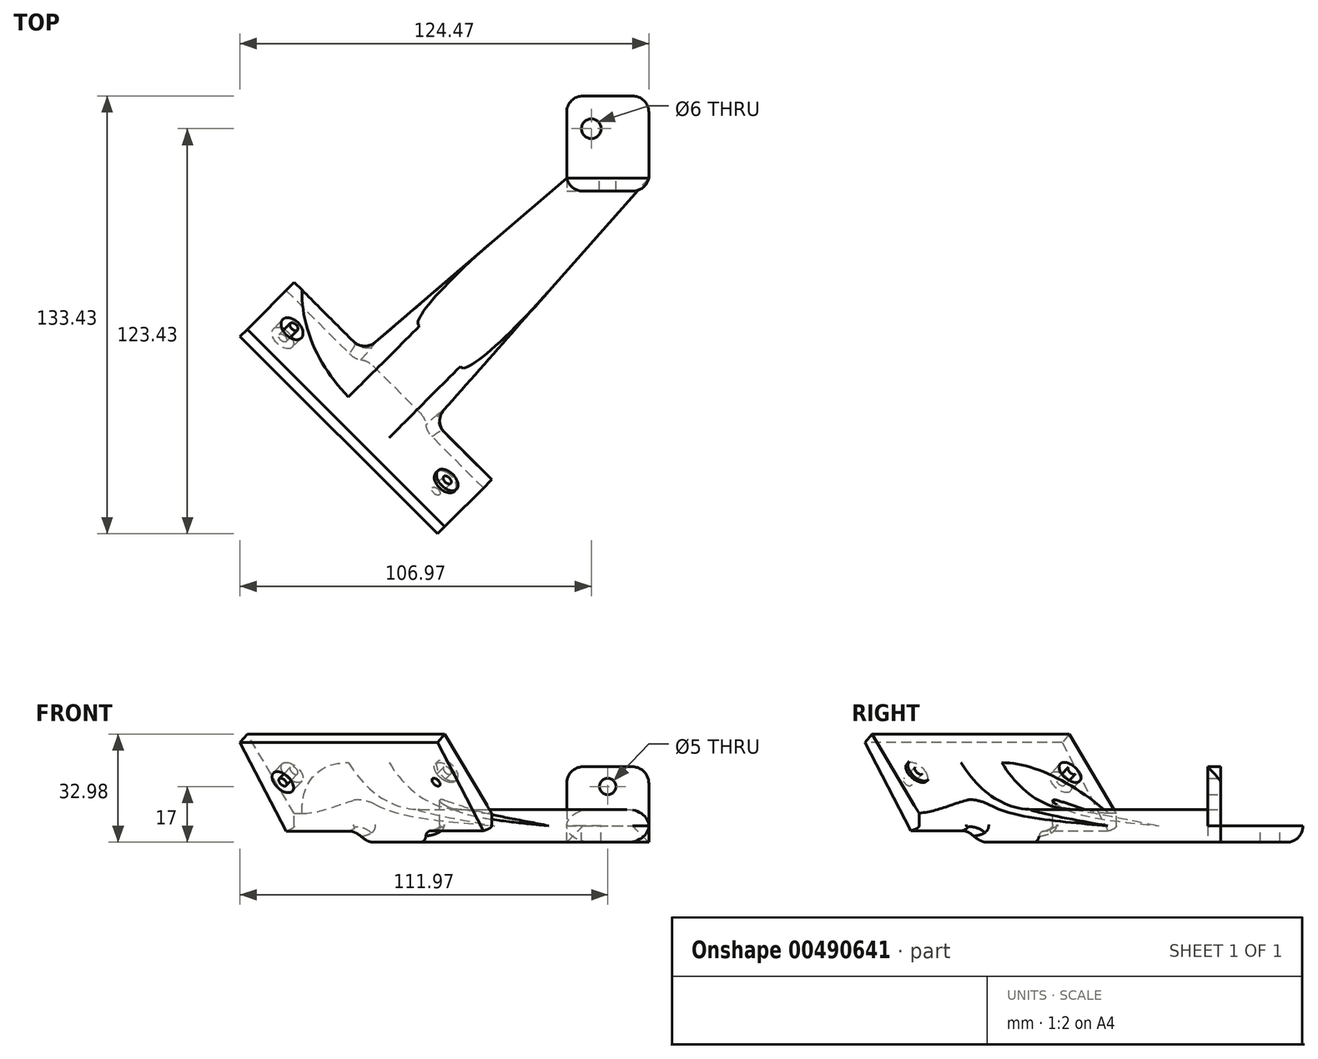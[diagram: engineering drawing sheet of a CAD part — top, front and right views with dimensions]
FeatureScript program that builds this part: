
annotation { "Feature Type Name" : "Feature", "Feature Type Description" : "" }
export const myFeature = defineFeature(function(context is Context, id is Id, definition is map)
    precondition{}
    {
        {
            var Q0;
            Q0=qCreatedBy(makeId("Top.planeOp"),FACE);
            var sketch = newSketch(context, id + "F0", { "sketchPlane" : qUnion([Q0])});
            skLineSegment(sketch, "E0.bottom", {"start": v(-12.5, 0) * mm, "end": v(12.5, 0) * mm});
            skLineSegment(sketch, "E0.top", {"start": v(-12.5, 25) * mm, "end": v(12.5, 25) * mm});
            skLineSegment(sketch, "E0.left", {"start": v(-12.5, 0) * mm, "end": v(-12.5, 25) * mm});
            skLineSegment(sketch, "E0.right", {"start": v(12.5, 0) * mm, "end": v(12.5, 25) * mm});
            skCircle(sketch, "E1", {"center": v(-5, 15) * mm, "radius": 3 * mm});
            skLineSegment(sketch, "E2.top", {"start": v(-12.5, -4) * mm, "end": v(12.5, -4) * mm});
            skLineSegment(sketch, "E2.left", {"start": v(-12.5, 0) * mm, "end": v(-12.5, -4) * mm});
            skLineSegment(sketch, "E2.right", {"start": v(12.5, 0) * mm, "end": v(12.5, -4) * mm});
            skSolve(sketch);
        }
        {
            var Q0;
            Q0=makeQuery(id+"F0.imprint","IMPRINT",FACE,{"disambiguationData":[TD([[makeQuery(id+"F0.imprint","IMPRINT",EDGE,{"derivedFrom":sQuery(id+"F0.wireOp",EDGE,"E0.top")}),-1.0]])]});
            extrude(context, id + "F1", {"entities" : qUnion([Q0]), "oppositeDirection" : true, "depth" : 5 * mm});
        }
        {
            var Q0;
            Q0=makeQuery(id+"F0.imprint","IMPRINT",FACE,{"disambiguationData":[TD([[makeQuery(id+"F0.imprint","IMPRINT",EDGE,{"derivedFrom":sQuery(id+"F0.wireOp",EDGE,"E0.bottom")}),-1.0]])]});
            extrude(context, id + "F2", {"entities" : qUnion([Q0]), "depth" : 18 * mm});
        }
        {
            var Q0;
            Q0=makeQuery(id+"F2.opExtrude","CAP_FACE",FACE,{"disambiguationData":[OSD([sQuery(id+"F0.wireOp",EDGE,"E0.bottom"),sQuery(id+"F0.wireOp",EDGE,"E2.top"),sQuery(id+"F0.wireOp",EDGE,"E2.left"),sQuery(id+"F0.wireOp",EDGE,"E2.right")])],"isStart":true});
            extrude(context, id + "F3", {"entities" : qUnion([Q0]), "depth" : 5 * mm});
        }
        {
            var Q0;
            Q0=makeQuery(id+"F2.opExtrude","SWEPT_FACE",FACE,{"disambiguationData":[OSD([sQuery(id+"F0.wireOp",EDGE,"E0.bottom")])]});
            var sketch = newSketch(context, id + "F4", { "sketchPlane" : qUnion([Q0])});
            skCircle(sketch, "E3", {"center": v(0, 12) * mm, "radius": 2.5 * mm});
            skSolve(sketch);
        }
        {
            var Q0;
            Q0=makeQuery(id+"F4.imprint","IMPRINT",FACE,{"disambiguationData":[TD([[makeQuery(id+"F4.imprint","IMPRINT",EDGE,{"derivedFrom":sQuery(id+"F4.wireOp",EDGE,"E3")}),1.0]])]});
            extrude(context, id + "F5", {"entities" : qUnion([Q0]), "operationType" : NewBodyOperationType.REMOVE, "oppositeDirection" : true, "depth" : 4 * mm});
        }
        {
            var Q0;
            Q0=qCreatedBy(makeId("Top.planeOp"),FACE);
            var sketch = newSketch(context, id + "F6", { "sketchPlane" : qUnion([Q0])});
            skLineSegment(sketch, "E4", {"start": v(0, 0) * mm, "end": v(-63.64, -63.64) * mm});
            skLineSegment(sketch, "E5", {"start": v(0, 0) * mm, "end": v(-12.5, 0) * mm});
            skLineSegment(sketch, "E6", {"start": v(-74.25, -53.03) * mm, "end": v(-63.64, -63.64) * mm});
            skLineSegment(sketch, "E7.MirrorCS", {"start": v(-53.03, -74.25) * mm, "end": v(-63.64, -63.64) * mm});
            skLineSegment(sketch, "E8", {"start": v(0, 0) * mm, "end": v(12.5, 0) * mm});
            skLineSegment(sketch, "E9", {"start": v(-74.25, -53.03) * mm, "end": v(-12.5, 0) * mm});
            skLineSegment(sketch, "E10", {"start": v(-53.03, -74.25) * mm, "end": v(12.5, 0) * mm});
            skSolve(sketch);
        }
        {
            var Q0;
            Q0=makeQuery(id+"F6.imprint","IMPRINT",FACE,{"disambiguationData":[TD([[makeQuery(id+"F6.imprint","IMPRINT",EDGE,{"derivedFrom":sQuery(id+"F6.wireOp",EDGE,"E4")}),-1.0]])]});
            var Q1;
            Q1=makeQuery(id+"F6.imprint","IMPRINT",FACE,{"disambiguationData":[TD([[makeQuery(id+"F6.imprint","IMPRINT",EDGE,{"derivedFrom":sQuery(id+"F6.wireOp",EDGE,"E4")}),1.0]])]});
            extrude(context, id + "F7", {"entities" : qUnion([Q0, Q1]), "endBound" : BoundingType.SYMMETRIC, "oppositeDirection" : true, "depth" : 10 * mm});
        }
        {
            var Q0;
            Q0=makeQuery(id+"F7.opExtrude","SWEPT_FACE",FACE,{"disambiguationData":[OSD([sQuery(id+"F6.wireOp",EDGE,"E6"),sQuery(id+"F6.wireOp",EDGE,"E7.MirrorCS")])]});
            var sketch = newSketch(context, id + "F8", { "sketchPlane" : qUnion([Q0])});
            skLineSegment(sketch, "E11.bottom", {"start": v(15, -5) * mm, "end": v(-15, -5) * mm});
            skLineSegment(sketch, "E11.top", {"start": v(15, 5) * mm, "end": v(-15, 5) * mm});
            skLineSegment(sketch, "E11.left", {"start": v(15, -5) * mm, "end": v(15, 5) * mm});
            skLineSegment(sketch, "E11.right", {"start": v(-15, -5) * mm, "end": v(-15, 5) * mm});
            skSolve(sketch);
        }
        {
            var Q0;
            Q0=makeQuery(id+"F8.imprint","IMPRINT",FACE,{"disambiguationData":[TD([[makeQuery(id+"F8.imprint","IMPRINT",EDGE,{"derivedFrom":sQuery(id+"F8.wireOp",EDGE,"E11.bottom")}),1.0]])]});
            extrude(context, id + "F9", {"entities" : qUnion([Q0]), "operationType" : NewBodyOperationType.ADD, "depth" : 1 * mm});
        }
        {
            var Q0;
            Q0=makeQuery(id+"F9.opExtrude","SWEPT_FACE",FACE,{"disambiguationData":[OSD([sQuery(id+"F8.wireOp",EDGE,"E11.left")])]});
            var sketch = newSketch(context, id + "F10", { "sketchPlane" : qUnion([Q0])});
            skLineSegment(sketch, "E12", {"start": v(-91, 5) * mm, "end": v(-110.28, 27.98) * mm});
            skLineSegment(sketch, "E13", {"start": v(-110.28, 27.98) * mm, "end": v(-113.35, 25.41) * mm});
            skLineSegment(sketch, "E14", {"start": v(-113.35, 25.41) * mm, "end": v(-91, -5) * mm});
            skSolve(sketch);
        }
        {
            var Q0;
            Q0=makeQuery(id+"F10.imprint","IMPRINT",FACE,{"disambiguationData":[TD([[makeQuery(id+"F10.imprint","IMPRINT",EDGE,{"derivedFrom":sQuery(id+"F10.wireOp",EDGE,"E12")}),1.0]])]});
            var Q1;
            Q1=makeQuery(id+"F9.opExtrude","SWEPT_FACE",FACE,{"disambiguationData":[OSD([sQuery(id+"F8.wireOp",EDGE,"E11.right")])]});
            extrude(context, id + "F11", {"entities" : qUnion([Q0]), "operationType" : NewBodyOperationType.ADD, "endBound" : BoundingType.UP_TO_SURFACE, "oppositeDirection" : true, "endBoundEntityFace" : qUnion([Q1]), "depth" : 25 * mm});
        }
        {
            var Q0;
            Q0=makeQuery(id+"F1.opExtrude","CAP_EDGE",EDGE,{"disambiguationData":[OSD([sQuery(id+"F0.wireOp",EDGE,"E0.top")])],"isStart":false});
            var Q1;
            Q1=makeQuery(id+"F2.opExtrude","SWEPT_EDGE",EDGE,{"disambiguationData":[OSD([sQuery(id+"F0.wireOp",EDGE,"E2.top"),sQuery(id+"F0.wireOp",EDGE,"E2.right")])]});
            var Q2;
            Q2=makeQuery(id+"F7.opExtrude","CAP_EDGE",EDGE,{"disambiguationData":[OSD([sQuery(id+"F6.wireOp",EDGE,"E9")])],"isStart":false});
            var Q3;
            Q3=makeQuery(id+"F7.opExtrude","CAP_EDGE",EDGE,{"disambiguationData":[OSD([sQuery(id+"F6.wireOp",EDGE,"E9")])],"isStart":true});
            var Q4;
            Q4=makeQuery(id+"F7.opExtrude","CAP_EDGE",EDGE,{"disambiguationData":[OSD([sQuery(id+"F6.wireOp",EDGE,"E10")])],"isStart":false});
            var Q5;
            Q5=makeQuery(id+"F3.opExtrude","SWEPT_EDGE",EDGE,{"disambiguationData":[OSD([sQuery(id+"F0.wireOp",EDGE,"E2.top"),sQuery(id+"F0.wireOp",EDGE,"E2.right")])]});
            var Q6;
            Q6=makeQuery(id+"F2.opExtrude","CAP_EDGE",EDGE,{"disambiguationData":[OSD([sQuery(id+"F0.wireOp",EDGE,"E2.left")])],"isStart":false});
            var Q7;
            Q7=makeQuery(id+"F1.opExtrude","SWEPT_EDGE",EDGE,{"disambiguationData":[OSD([sQuery(id+"F0.wireOp",EDGE,"E0.top"),sQuery(id+"F0.wireOp",EDGE,"E0.right")])]});
            var Q8;
            Q8=makeQuery(id+"F1.opExtrude","SWEPT_EDGE",EDGE,{"disambiguationData":[OSD([sQuery(id+"F0.wireOp",EDGE,"E0.top"),sQuery(id+"F0.wireOp",EDGE,"E0.left")])]});
            var Q9;
            Q9=makeQuery(id+"F7.opExtrude","CAP_EDGE",EDGE,{"disambiguationData":[OSD([sQuery(id+"F6.wireOp",EDGE,"E10")])],"isStart":true});
            var Q10;
            Q10=makeQuery(id+"F2.opExtrude","CAP_EDGE",EDGE,{"disambiguationData":[OSD([sQuery(id+"F0.wireOp",EDGE,"E2.right")])],"isStart":false});
            var Q11;
            Q11=makeQuery(id+"F2.opExtrude","SWEPT_EDGE",EDGE,{"disambiguationData":[OSD([sQuery(id+"F0.wireOp",EDGE,"E2.top"),sQuery(id+"F0.wireOp",EDGE,"E2.left")])]});
            fillet(context, id + "F12", {"entities" : qUnion([Q0, Q1, Q2, Q3, Q4, Q5, Q6, Q7, Q8, Q9, Q10, Q11]), "radius" : 5 * mm, "tangentPropagation" : true, "allowEdgeOverflow" : false});
        }
        {
            var Q0;
            {var subQ0=sQuery(id+"F8.wireOp",EDGE,"E11.left");Q0=makeQuery(id+"F11.boolean.opBoolean","MERGE",FACE,{"derivedFrom":[makeQuery(id+"F9.opExtrude","SWEPT_FACE",FACE,{"disambiguationData":[OSD([subQ0])]}),makeQuery(id+"F11.opExtrude","CAP_FACE",FACE,{"disambiguationData":[OSD([subQ0,sQuery(id+"F10.wireOp",EDGE,"E12"),sQuery(id+"F10.wireOp",EDGE,"E13"),sQuery(id+"F10.wireOp",EDGE,"E14")])],"isStart":true})]});}
            extrude(context, id + "F13", {"entities" : qUnion([Q0]), "operationType" : NewBodyOperationType.ADD, "depth" : 25 * mm});
        }
        {
            var Q0;
            {var subQ0=sQuery(id+"F8.wireOp",EDGE,"E11.right");Q0=makeQuery(id+"F11.boolean.opBoolean","MERGE",FACE,{"derivedFrom":[makeQuery(id+"F9.opExtrude","SWEPT_FACE",FACE,{"disambiguationData":[OSD([subQ0])]}),makeQuery(id+"F11.opExtrude","CAP_FACE",FACE,{"disambiguationData":[OSD([subQ0])],"isStart":false})]});}
            extrude(context, id + "F14", {"entities" : qUnion([Q0]), "operationType" : NewBodyOperationType.ADD, "depth" : 30 * mm});
        }
        {
            var Q0;
            {var subQ0=sQuery(id+"F10.wireOp",EDGE,"E14");Q0=makeQuery(id+"F14.boolean.opBoolean","MERGE",FACE,{"derivedFrom":[makeQuery(id+"F13.boolean.opBoolean","MERGE",FACE,{"derivedFrom":[makeQuery(id+"F11.opExtrude","SWEPT_FACE",FACE,{"disambiguationData":[OSD([subQ0])]}),makeQuery(id+"F13.opExtrude","SWEPT_FACE",FACE,{"disambiguationData":[OSD([subQ0])]})]}),makeQuery(id+"F14.opExtrude","SWEPT_FACE",FACE,{"disambiguationData":[OSD([sQuery(id+"F8.wireOp",EDGE,"E11.right"),subQ0])]})]});}
            var sketch = newSketch(context, id + "F15", { "sketchPlane" : qUnion([Q0])});
            skLineSegment(sketch, "E15", {"start": v(-46.79, 74.1) * mm, "end": v(-39.14, 61.2) * mm});
            skLineSegment(sketch, "E16", {"start": v(-39.14, 61.2) * mm, "end": v(-10.75, 78) * mm});
            skCircle(sketch, "E17", {"center": v(-10.75, 78) * mm, "radius": 1.5 * mm});
            skCircle(sketch, "E18.MirrorC", {"center": v(-67.54, 44.38) * mm, "radius": 1.5 * mm});
            skCircle(sketch, "E19", {"center": v(-67.54, 44.38) * mm, "radius": 4 * mm});
            skCircle(sketch, "E20", {"center": v(-10.75, 78) * mm, "radius": 4 * mm});
            skSolve(sketch);
        }
        {
            var Q0;
            Q0=makeQuery(id+"F15.imprint","IMPRINT",FACE,{"disambiguationData":[TD([[makeQuery(id+"F15.imprint","IMPRINT",EDGE,{"derivedFrom":sQuery(id+"F15.wireOp",EDGE,"E18.MirrorC")}),1.0]])]});
            var Q1;
            Q1=makeQuery(id+"F15.imprint","IMPRINT",FACE,{"disambiguationData":[TD([[makeQuery(id+"F15.imprint","IMPRINT",EDGE,{"derivedFrom":sQuery(id+"F15.wireOp",EDGE,"E18.MirrorC")}),-1.0]])]});
            var Q2;
            Q2=makeQuery(id+"F15.imprint","IMPRINT",FACE,{"disambiguationData":[TD([[makeQuery(id+"F15.imprint","IMPRINT",EDGE,{"derivedFrom":sQuery(id+"F15.wireOp",EDGE,"E17")}),-1.0]])]});
            var Q3;
            Q3=makeQuery(id+"F15.imprint","IMPRINT",FACE,{"disambiguationData":[TD([[makeQuery(id+"F15.imprint","IMPRINT",EDGE,{"derivedFrom":sQuery(id+"F15.wireOp",EDGE,"E17")}),1.0]])]});
            extrude(context, id + "F16", {"entities" : qUnion([Q0, Q1, Q2, Q3]), "operationType" : NewBodyOperationType.ADD, "oppositeDirection" : true, "depth" : 6 * mm});
        }
        {
            var Q0;
            Q0=makeQuery(id+"F15.imprint","IMPRINT",FACE,{"disambiguationData":[TD([[makeQuery(id+"F15.imprint","IMPRINT",EDGE,{"derivedFrom":sQuery(id+"F15.wireOp",EDGE,"E18.MirrorC")}),-1.0]])]});
            var Q1;
            Q1=makeQuery(id+"F15.imprint","IMPRINT",FACE,{"disambiguationData":[TD([[makeQuery(id+"F15.imprint","IMPRINT",EDGE,{"derivedFrom":sQuery(id+"F15.wireOp",EDGE,"E17")}),1.0]])]});
            extrude(context, id + "F17", {"entities" : qUnion([Q0, Q1]), "operationType" : NewBodyOperationType.REMOVE, "endBound" : BoundingType.THROUGH_ALL, "oppositeDirection" : true, "depth" : 25 * mm});
        }
        {
            var Q0;
            {var subQ0=sQuery(id+"F8.wireOp",EDGE,"E11.top");Q0=makeQuery(id+"F11.boolean.opBoolean","MERGE",EDGE,{"derivedFrom":[makeQuery(id+"F9.opExtrude","CAP_EDGE",EDGE,{"disambiguationData":[OSD([subQ0])],"isStart":false}),makeQuery(id+"F11.opExtrude","SWEPT_EDGE",EDGE,{"disambiguationData":[OSD([subQ0,sQuery(id+"F8.wireOp",EDGE,"E11.left"),sQuery(id+"F10.wireOp",EDGE,"E12")])]})]});}
            fillet(context, id + "F18", {"entities" : qUnion([Q0]), "radius" : 40 * mm, "tangentPropagation" : true, "allowEdgeOverflow" : false});
        }
        {
            var Q0;
            {var subQ0=sQuery(id+"F8.wireOp",EDGE,"E11.left");var subQ1=sQuery(id+"F6.wireOp",EDGE,"E10");var subQ2=sQuery(id+"F6.wireOp",EDGE,"E7.MirrorCS");Q0=makeQuery(id+"F13.boolean.opBoolean","MERGE",EDGE,{"derivedFrom":[makeQuery(id+"F9.boolean.opBoolean","MERGE",EDGE,{"derivedFrom":[makeQuery(id+"F7.opExtrude","SWEPT_EDGE",EDGE,{"disambiguationData":[OSD([subQ2,subQ1])]}),makeQuery(id+"F9.opExtrude","CAP_EDGE",EDGE,{"disambiguationData":[OSD([subQ0])],"isStart":true})]}),makeQuery(id+"F13.opExtrude","CAP_EDGE",EDGE,{"disambiguationData":[OSD([subQ2,subQ1,subQ0])],"isStart":true})]});}
            var Q1;
            {var subQ0=sQuery(id+"F8.wireOp",EDGE,"E11.right");var subQ1=sQuery(id+"F6.wireOp",EDGE,"E9");var subQ2=sQuery(id+"F6.wireOp",EDGE,"E6");Q1=makeQuery(id+"F14.boolean.opBoolean","MERGE",EDGE,{"derivedFrom":[makeQuery(id+"F9.boolean.opBoolean","MERGE",EDGE,{"derivedFrom":[makeQuery(id+"F7.opExtrude","SWEPT_EDGE",EDGE,{"disambiguationData":[OSD([subQ2,subQ1])]}),makeQuery(id+"F9.opExtrude","CAP_EDGE",EDGE,{"disambiguationData":[OSD([subQ0])],"isStart":true})]}),makeQuery(id+"F14.opExtrude","CAP_EDGE",EDGE,{"disambiguationData":[OSD([subQ2,subQ1,subQ0])],"isStart":true})]});}
            fillet(context, id + "F19", {"entities" : qUnion([Q0, Q1]), "radius" : 5 * mm, "tangentPropagation" : true, "allowEdgeOverflow" : false});
        }
    });
